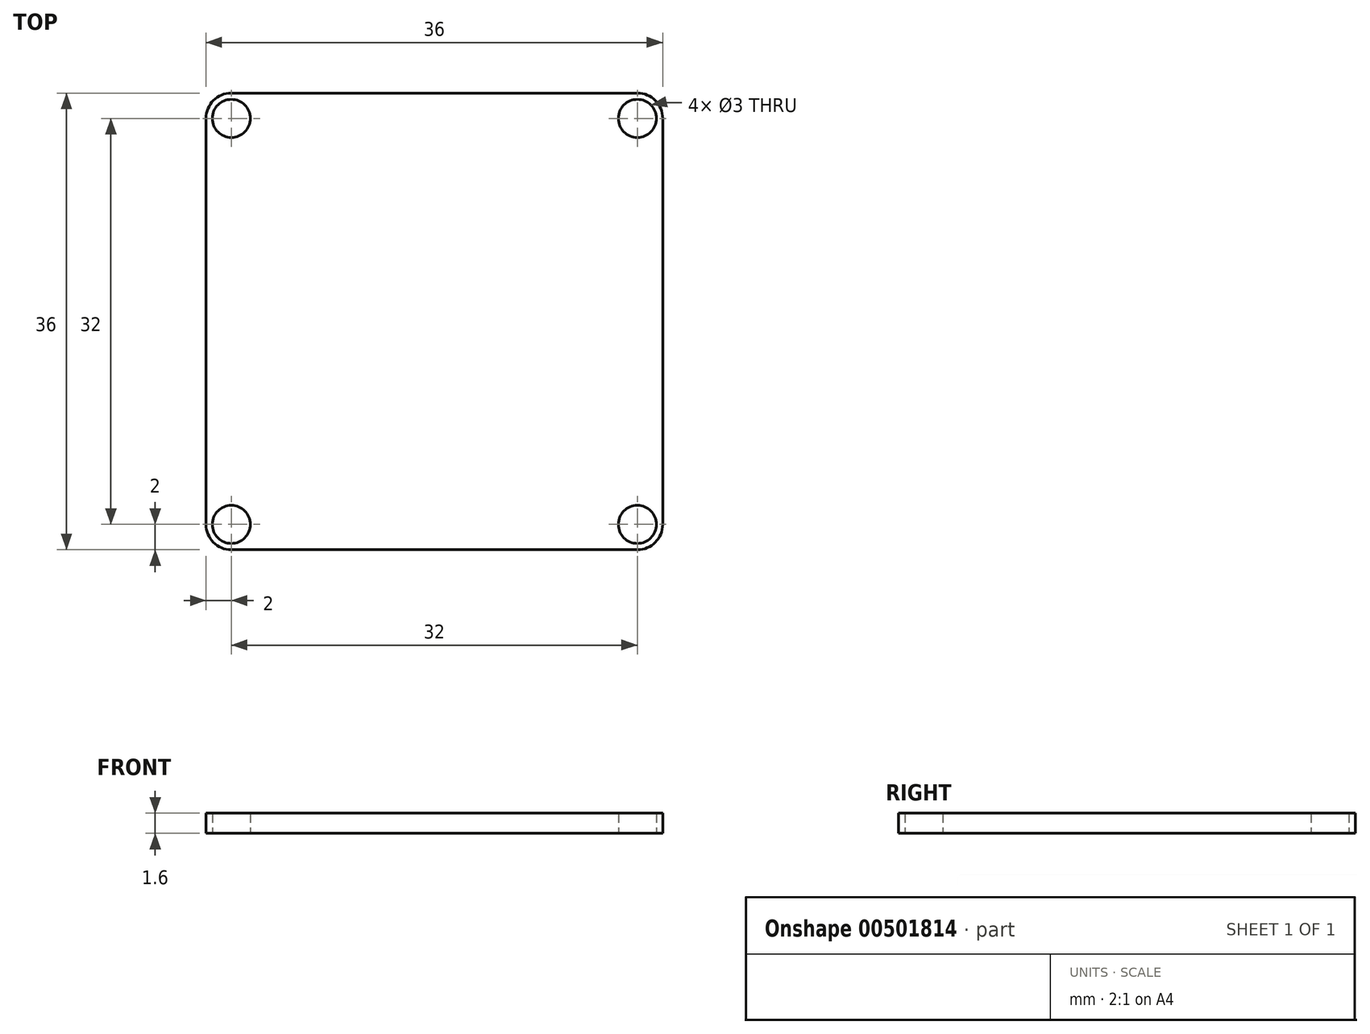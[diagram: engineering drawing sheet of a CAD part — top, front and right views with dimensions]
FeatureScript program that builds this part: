
annotation { "Feature Type Name" : "Feature", "Feature Type Description" : "" }
export const myFeature = defineFeature(function(context is Context, id is Id, definition is map)
    precondition{}
    {
        {
            var Q0;
            Q0=qCreatedBy(makeId("Top.planeOp"),FACE);
            var sketch = newSketch(context, id + "F0", { "sketchPlane" : qUnion([Q0])});
            skLineSegment(sketch, "E0.bottom", {"start": v(18, 18) * mm, "end": v(-18, 18) * mm});
            skLineSegment(sketch, "E0.top", {"start": v(18, -18) * mm, "end": v(-18, -18) * mm});
            skLineSegment(sketch, "E0.left", {"start": v(18, 18) * mm, "end": v(18, -18) * mm});
            skLineSegment(sketch, "E0.right", {"start": v(-18, 18) * mm, "end": v(-18, -18) * mm});
            skPoint(sketch, "E0.middle", {"position": v(0, 0) * mm});
            skLineSegment(sketch, "E1", {"start": v(0, 18) * mm, "end": v(0, -18) * mm, "construction": true});
            skLineSegment(sketch, "E2", {"start": v(-18, 0) * mm, "end": v(18, 0) * mm, "construction": true});
            skCircle(sketch, "E3", {"center": v(-16, 16) * mm, "radius": 1.5 * mm});
            skCircle(sketch, "E4.MirrorC", {"center": v(16, 16) * mm, "radius": 1.5 * mm});
            skLineSegment(sketch, "E5.MirrorCS", {"start": v(18, 0) * mm, "end": v(-18, 0) * mm, "construction": true});
            skCircle(sketch, "E6.MirrorC", {"center": v(-16, -16) * mm, "radius": 1.5 * mm});
            skCircle(sketch, "E7.MirrorC", {"center": v(16, -16) * mm, "radius": 1.5 * mm});
            skSolve(sketch);
        }
        {
            var Q0;
            Q0=qSketchRegion(id+"F0",true);
            extrude(context, id + "F1", {"entities" : qUnion([Q0]), "depth" : 1.6 * mm});
        }
        {
            var Q0;
            Q0=makeQuery(id+"F1.opExtrude","SWEPT_EDGE",EDGE,{"disambiguationData":[OSD([sQuery(id+"F0.wireOp",EDGE,"E0.bottom"),sQuery(id+"F0.wireOp",EDGE,"E0.right")])]});
            var Q1;
            Q1=makeQuery(id+"F1.opExtrude","SWEPT_EDGE",EDGE,{"disambiguationData":[OSD([sQuery(id+"F0.wireOp",EDGE,"E0.bottom"),sQuery(id+"F0.wireOp",EDGE,"E0.left")])]});
            var Q2;
            Q2=makeQuery(id+"F1.opExtrude","SWEPT_EDGE",EDGE,{"disambiguationData":[OSD([sQuery(id+"F0.wireOp",EDGE,"E0.top"),sQuery(id+"F0.wireOp",EDGE,"E0.left")])]});
            var Q3;
            Q3=makeQuery(id+"F1.opExtrude","SWEPT_EDGE",EDGE,{"disambiguationData":[OSD([sQuery(id+"F0.wireOp",EDGE,"E0.top"),sQuery(id+"F0.wireOp",EDGE,"E0.right")])]});
            fillet(context, id + "F2", {"entities" : qUnion([Q0, Q1, Q2, Q3]), "radius" : 2 * mm, "tangentPropagation" : true, "allowEdgeOverflow" : false});
        }
    });
